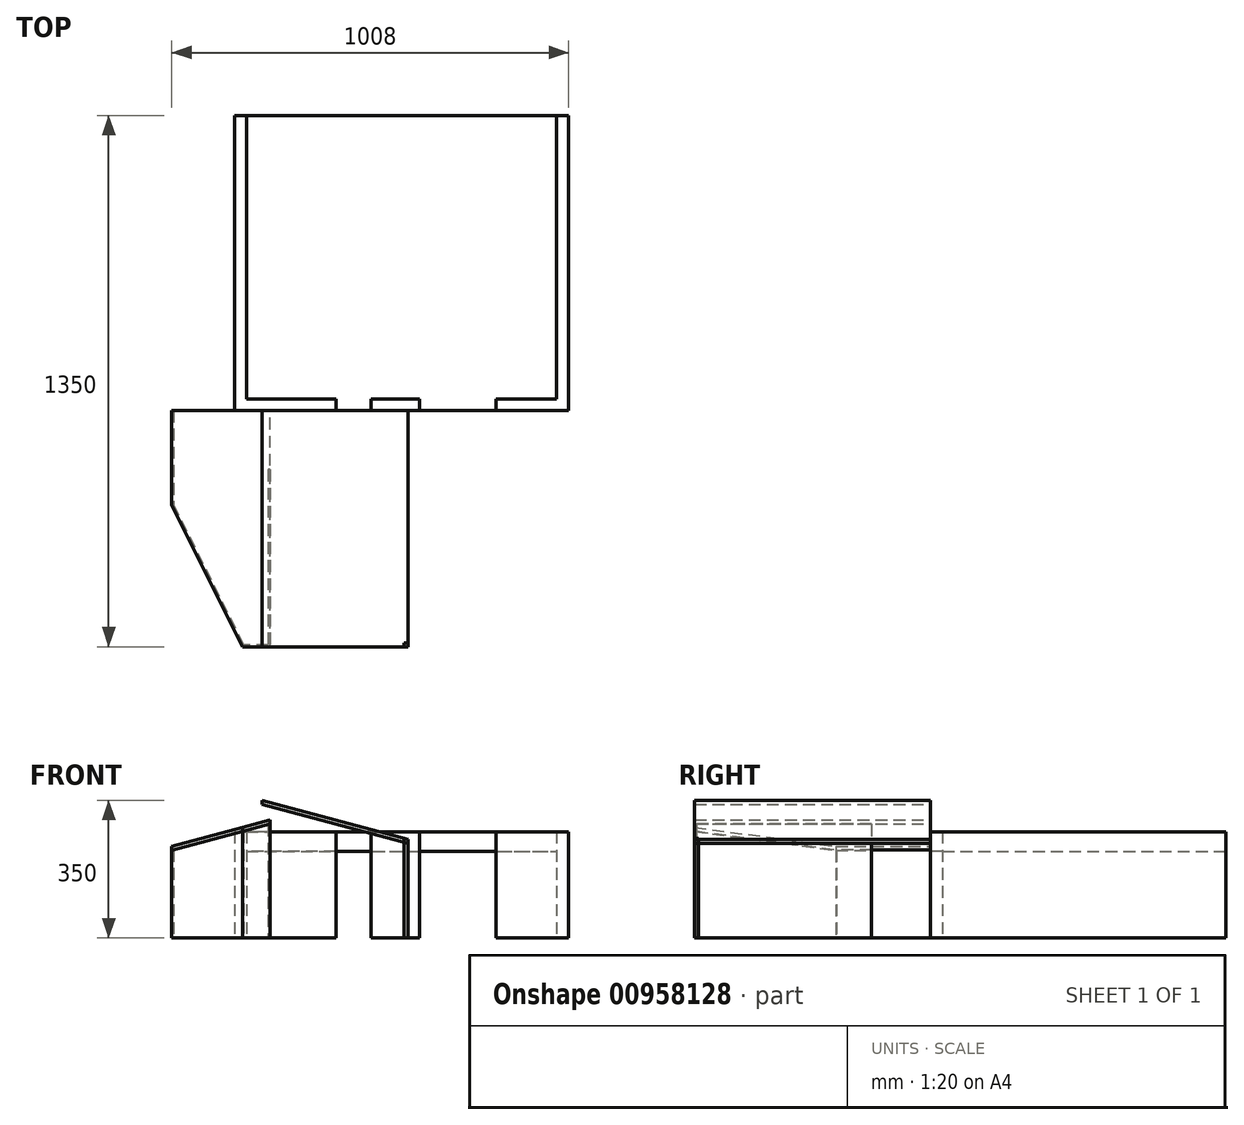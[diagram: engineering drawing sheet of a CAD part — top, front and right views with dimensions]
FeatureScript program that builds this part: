
annotation { "Feature Type Name" : "Feature", "Feature Type Description" : "" }
export const myFeature = defineFeature(function(context is Context, id is Id, definition is map)
    precondition{}
    {
        {
            var Q0;
            Q0=qCreatedBy(makeId("Top.planeOp"),FACE);
            var sketch = newSketch(context, id + "F0", { "sketchPlane" : qUnion([Q0])});
            skLineSegment(sketch, "E0", {"start": v(0, 0) * mm, "end": v(-600, 0) * mm});
            skLineSegment(sketch, "E1", {"start": v(-600, 0) * mm, "end": v(-600, -240) * mm});
            skLineSegment(sketch, "E2", {"start": v(-600, -240) * mm, "end": v(-420, -600) * mm});
            skLineSegment(sketch, "E3", {"start": v(-420, -600) * mm, "end": v(0, -600) * mm});
            skLineSegment(sketch, "E4", {"start": v(0, -600) * mm, "end": v(0, 0) * mm});
            skLineSegment(sketch, "E5.bottom", {"start": v(0, -600) * mm, "end": v(-10, -600) * mm});
            skLineSegment(sketch, "E5.top", {"start": v(0, -590) * mm, "end": v(-10, -590) * mm});
            skLineSegment(sketch, "E5.left", {"start": v(0, -600) * mm, "end": v(0, -590) * mm});
            skLineSegment(sketch, "E5.right", {"start": v(-10, -600) * mm, "end": v(-10, -590) * mm});
            skLineSegment(sketch, "E6", {"start": v(-595, -238.82) * mm, "end": v(-595, 0) * mm});
            skLineSegment(sketch, "E7", {"start": v(-350, -600) * mm, "end": v(-350, -150) * mm});
            skLineSegment(sketch, "E8", {"start": v(-420, -600) * mm, "end": v(-600, -600) * mm});
            skLineSegment(sketch, "E9", {"start": v(-600, -600) * mm, "end": v(-600, -240) * mm});
            skLineSegment(sketch, "E10", {"start": v(-416.9, -595) * mm, "end": v(-355, -595) * mm});
            skLineSegment(sketch, "E11", {"start": v(-355, -595) * mm, "end": v(-355, -150) * mm});
            skLineSegment(sketch, "E12", {"start": v(-350, -600) * mm, "end": v(-483.9, -600) * mm});
            skLineSegment(sketch, "E13", {"start": v(-595, -238.82) * mm, "end": v(-416.9, -595) * mm});
            skLineSegment(sketch, "E14", {"start": v(-355, -150) * mm, "end": v(-350, -150) * mm});
            skLineSegment(sketch, "E15.bottom", {"start": v(-440, 0) * mm, "end": v(408, 0) * mm});
            skLineSegment(sketch, "E15.top", {"start": v(-440, 750) * mm, "end": v(408, 750) * mm});
            skLineSegment(sketch, "E15.left", {"start": v(-440, 0) * mm, "end": v(-440, 750) * mm});
            skLineSegment(sketch, "E15.right", {"start": v(408, 0) * mm, "end": v(408, 750) * mm});
            skLineSegment(sketch, "E16", {"start": v(-355, -450) * mm, "end": v(-489.4, -450) * mm});
            skLineSegment(sketch, "E17", {"start": v(-489.4, -450) * mm, "end": v(-486.9, -455) * mm});
            skLineSegment(sketch, "E18", {"start": v(-486.9, -455) * mm, "end": v(-355, -455) * mm});
            skLineSegment(sketch, "E19", {"start": v(-355, -455) * mm, "end": v(-350, -455) * mm});
            skLineSegment(sketch, "E20", {"start": v(-355, -595) * mm, "end": v(-350, -595) * mm});
            skLineSegment(sketch, "E21", {"start": v(-420, -600) * mm, "end": v(-196.4, -1047.21) * mm, "construction": true});
            skLineSegment(sketch, "E22", {"start": v(-183, 30) * mm, "end": v(-183, 0) * mm});
            skLineSegment(sketch, "E23", {"start": v(-183, 0) * mm, "end": v(-93, 0) * mm});
            skLineSegment(sketch, "E24", {"start": v(-93, 0) * mm, "end": v(-93, 30) * mm});
            skLineSegment(sketch, "E25", {"start": v(-93, 30) * mm, "end": v(30, 30) * mm});
            skLineSegment(sketch, "E26", {"start": v(30, 30) * mm, "end": v(30, 0) * mm});
            skLineSegment(sketch, "E27", {"start": v(224, 0) * mm, "end": v(224, 30) * mm});
            skLineSegment(sketch, "E28", {"start": v(224, 30) * mm, "end": v(378, 30) * mm});
            skLineSegment(sketch, "E29", {"start": v(378, 30) * mm, "end": v(378, 750) * mm});
            skLineSegment(sketch, "E30", {"start": v(-183, 30) * mm, "end": v(-410, 30) * mm});
            skLineSegment(sketch, "E31", {"start": v(-410, 30) * mm, "end": v(-410, 750) * mm});
            skSolve(sketch);
        }
        {
            var Q0;
            Q0=qCreatedBy(makeId("Front.planeOp"),FACE);
            var sketch = newSketch(context, id + "F1", { "sketchPlane" : qUnion([Q0])});
            skLineSegment(sketch, "E32", {"start": v(-600, 233.01) * mm, "end": v(-350, 300) * mm});
            skLineSegment(sketch, "E33", {"start": v(-370, 339.65) * mm, "end": v(0, 240.5) * mm});
            skLineSegment(sketch, "E34", {"start": v(-350, 300) * mm, "end": v(-350, 87.94) * mm, "construction": true});
            skLineSegment(sketch, "E35", {"start": v(0, 250.86) * mm, "end": v(0, 240.5) * mm});
            skLineSegment(sketch, "E36", {"start": v(0, 250.86) * mm, "end": v(-370, 350) * mm});
            skLineSegment(sketch, "E37", {"start": v(-350, 289.65) * mm, "end": v(-600, 222.66) * mm});
            skLineSegment(sketch, "E38", {"start": v(-600, 222.66) * mm, "end": v(-600, 233.01) * mm});
            skLineSegment(sketch, "E39", {"start": v(-370, 350) * mm, "end": v(-370, 339.65) * mm});
            skLineSegment(sketch, "E40", {"start": v(-350, 300) * mm, "end": v(-350, 289.65) * mm});
            skSolve(sketch);
        }
        {
            var Q0;
            Q0=makeQuery(id+"F1.imprint","IMPRINT",FACE,{"disambiguationData":[TD([[makeQuery(id+"F1.imprint","IMPRINT",EDGE,{"derivedFrom":sQuery(id+"F1.wireOp",EDGE,"E32")}),-1.0]])]});
            var Q1;
            Q1=makeQuery(id+"F1.imprint","IMPRINT",FACE,{"disambiguationData":[TD([[makeQuery(id+"F1.imprint","IMPRINT",EDGE,{"derivedFrom":sQuery(id+"F1.wireOp",EDGE,"E33")}),1.0]])]});
            var Q2;
            Q2=makeQuery(id+"F3.opExtrude","SWEPT_FACE",FACE,{"disambiguationData":[OSD([sQuery(id+"F0.wireOp",EDGE,"E3")])]});
            var Q3;
            Q3=sQuery(id+"F0.wireOp",VERTEX,"E7.start");
            extrude(context, id + "F2", {"entities" : qUnion([Q0, Q1]), "endBound" : BoundingType.UP_TO_VERTEX, "depth" : 25 * mm, "endBoundEntityFace" : qUnion([Q2]), "endBoundEntityVertex" : qUnion([Q3]), "offsetDistance" : 25 * mm});
        }
        {
            var Q0;
            {var subQ0=sQuery(id+"F0.wireOp",EDGE,"E14");Q0=makeQuery(id+"F0.imprint","IMPRINT",FACE,{"disambiguationData":[TD([[makeQuery(id+"F0.imprint","IMPRINT",EDGE,{"derivedFrom":subQ0}),-1.0]])]});}
            var Q1;
            {var subQ5=sQuery(id+"F0.wireOp",EDGE,"E1");Q1=makeQuery(id+"F0.imprint","IMPRINT",FACE,{"disambiguationData":[TD([[makeQuery(id+"F0.imprint","IMPRINT",EDGE,{"derivedFrom":subQ5}),1.0]])]});}
            var Q2;
            {var subQ0=sQuery(id+"F0.wireOp",EDGE,"E19");Q2=makeQuery(id+"F0.imprint","IMPRINT",FACE,{"disambiguationData":[TD([[makeQuery(id+"F0.imprint","IMPRINT",EDGE,{"derivedFrom":subQ0}),-1.0]])]});}
            var Q3;
            Q3=makeQuery(id+"F2.opExtrude","SWEPT_FACE",FACE,{"disambiguationData":[OSD([sQuery(id+"F1.wireOp",EDGE,"E37")])]});
            extrude(context, id + "F3", {"entities" : qUnion([Q0, Q1, Q2]), "endBound" : BoundingType.UP_TO_SURFACE, "depth" : 300 * mm, "endBoundEntityFace" : qUnion([Q3]), "offsetDistance" : 25 * mm});
        }
        {
            var Q0;
            {var subQ0=sQuery(id+"F0.wireOp",EDGE,"E2");Q0=makeQuery(id+"F0.imprint","IMPRINT",FACE,{"disambiguationData":[TD([[makeQuery(id+"F0.imprint","IMPRINT",EDGE,{"derivedFrom":subQ0}),-1.0]])]});}
            var Q1;
            Q1=makeQuery(id+"F2.opExtrude","SWEPT_FACE",FACE,{"disambiguationData":[OSD([sQuery(id+"F1.wireOp",EDGE,"E32")])]});
            extrude(context, id + "F4", {"entities" : qUnion([Q0]), "operationType" : NewBodyOperationType.REMOVE, "endBound" : BoundingType.THROUGH_ALL, "depth" : 25 * mm, "endBoundEntityFace" : qUnion([Q1]), "offsetDistance" : 25 * mm});
        }
        {
            var Q0;
            {var subQ3=sQuery(id+"F0.wireOp",EDGE,"E15.left");var subQ5=sQuery(id+"F0.wireOp",EDGE,"E15.right");Q0=qUnion([makeQuery(id+"F0.imprint","IMPRINT",FACE,{"disambiguationData":[TD([[makeQuery(id+"F0.imprint","IMPRINT",EDGE,{"derivedFrom":subQ5}),1.0]])]}),makeQuery(id+"F0.imprint","IMPRINT",FACE,{"disambiguationData":[TD([[makeQuery(id+"F0.imprint","IMPRINT",EDGE,{"derivedFrom":subQ3}),-1.0]])]})]);}
            var Q1;
            {var subQ4=sQuery(id+"F0.wireOp",EDGE,"E24");Q1=makeQuery(id+"F0.imprint","IMPRINT",FACE,{"disambiguationData":[TD([[makeQuery(id+"F0.imprint","IMPRINT",EDGE,{"derivedFrom":subQ4}),-1.0]])]});}
            extrude(context, id + "F5", {"entities" : qUnion([Q0, Q1]), "depth" : 270 * mm, "offsetDistance" : 25 * mm});
        }
        {
            var Q0;
            {var subQ4=sQuery(id+"F0.wireOp",EDGE,"E5.top");Q0=makeQuery(id+"F0.imprint","IMPRINT",FACE,{"disambiguationData":[TD([[makeQuery(id+"F0.imprint","IMPRINT",EDGE,{"derivedFrom":subQ4}),1.0]])]});}
            var Q1;
            Q1=makeQuery(id+"F2.opExtrude","SWEPT_FACE",FACE,{"disambiguationData":[OSD([sQuery(id+"F1.wireOp",EDGE,"E36")])]});
            extrude(context, id + "F6", {"entities" : qUnion([Q0]), "endBound" : BoundingType.UP_TO_SURFACE, "depth" : 25 * mm, "endBoundEntityFace" : qUnion([Q1]), "offsetDistance" : 25 * mm});
        }
        {
            var Q0;
            {var subQ4=sQuery(id+"F0.wireOp",EDGE,"E22");Q0=makeQuery(id+"F0.imprint","IMPRINT",FACE,{"disambiguationData":[TD([[makeQuery(id+"F0.imprint","IMPRINT",EDGE,{"derivedFrom":subQ4}),1.0]])]});}
            extrude(context, id + "F7", {"entities" : qUnion([Q0]), "depth" : 270 * mm, "offsetDistance" : 25 * mm, "hasSecondDirection" : true, "secondDirectionOppositeDirection" : false, "secondDirectionDepth" : 220 * mm});
        }
    });
